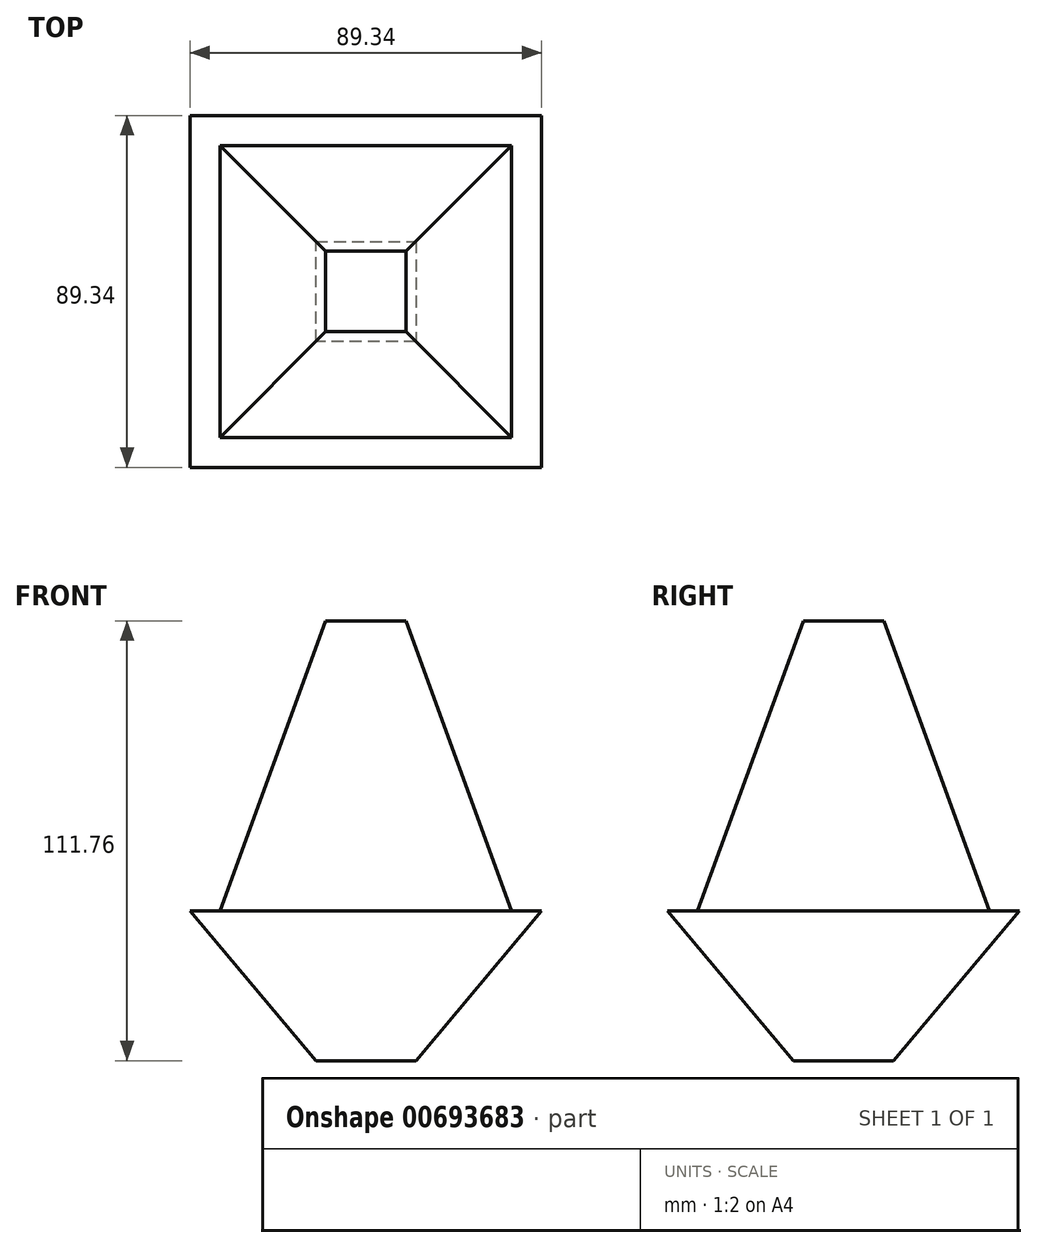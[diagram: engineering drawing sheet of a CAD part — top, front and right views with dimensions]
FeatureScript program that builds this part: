
annotation { "Feature Type Name" : "Feature", "Feature Type Description" : "" }
export const myFeature = defineFeature(function(context is Context, id is Id, definition is map)
    precondition{}
    {
        {
            var Q0;
            Q0=qCreatedBy(makeId("Top.planeOp"),FACE);
            var sketch = newSketch(context, id + "F0", { "sketchPlane" : qUnion([Q0])});
            skLineSegment(sketch, "E0.bottom", {"start": v(-12.7, 0) * mm, "end": v(12.7, 0) * mm});
            skLineSegment(sketch, "E0.top", {"start": v(-12.7, -25.4) * mm, "end": v(12.7, -25.4) * mm});
            skLineSegment(sketch, "E0.left", {"start": v(-12.7, 0) * mm, "end": v(-12.7, -25.4) * mm});
            skLineSegment(sketch, "E0.right", {"start": v(12.7, 0) * mm, "end": v(12.7, -25.4) * mm});
            skSolve(sketch);
        }
        {
            var Q0;
            Q0 = qSketchRegion(id + "F0", true);
            extrude(context, id + "F1", {"entities" : qUnion([Q0]), "depth" : 38.1 * mm, "offsetDistance" : 25.4 * mm, "hasDraft" : true, "draftAngle" : 40 * degree});
        }
        {
            var Q0;
            Q0=makeQuery(id+"F1.opExtrude","CAP_FACE",FACE,{"disambiguationData":[OSD([sQuery(id+"F0.wireOp",EDGE,"E0.bottom"),sQuery(id+"F0.wireOp",EDGE,"E0.top"),sQuery(id+"F0.wireOp",EDGE,"E0.left"),sQuery(id+"F0.wireOp",EDGE,"E0.right")])],"isStart":false});
            var sketch = newSketch(context, id + "F2", { "sketchPlane" : qUnion([Q0])});
            skLineSegment(sketch, "E1.0", {"start": v(-37.05, 24.35) * mm, "end": v(-37.05, -49.75) * mm});
            skLineSegment(sketch, "E1.1", {"start": v(37.05, 24.35) * mm, "end": v(-37.05, 24.35) * mm});
            skLineSegment(sketch, "E1.2", {"start": v(37.05, -49.75) * mm, "end": v(37.05, 24.35) * mm});
            skLineSegment(sketch, "E1.3", {"start": v(-37.05, -49.75) * mm, "end": v(37.05, -49.75) * mm});
            skSolve(sketch);
        }
        {
            var Q0;
            Q0 = qSketchRegion(id + "F2", true);
            extrude(context, id + "F3", {"entities" : qUnion([Q0]), "operationType" : NewBodyOperationType.ADD, "depth" : 73.66 * mm, "offsetDistance" : 25.4 * mm, "hasDraft" : true, "draftAngle" : 20 * degree, "draftPullDirection" : true});
        }
    });
